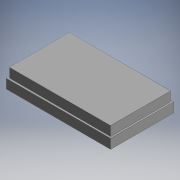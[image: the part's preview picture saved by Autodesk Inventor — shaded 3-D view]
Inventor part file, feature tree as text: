
AUTODESK INVENTOR PART (.ipt)
format: ipt  version: 2018 (Build 220112000, 112)  size: 109,568 bytes
history: native  units: in
note: dims shown in document units (in); Inventor stores cm internally (conversion verified against a paired STEP export)
features: extrude x2, other x2, projected_geometry x1
ambient origin geometry x8: Origin, YZ Plane, XZ Plane, XY Plane, X Axis, Y Axis, Z Axis, Center Point
bodies: Solid1 (feature_tree)
feature tree (5):
  extrude  "Base"  Depth=1.2992in
  extrude  "Inner Part"  Depth=0.7874in
  other  "Base Sketch"
  other  "Inner Part Sketch"
  projected_geometry  "Projected Loop1"
